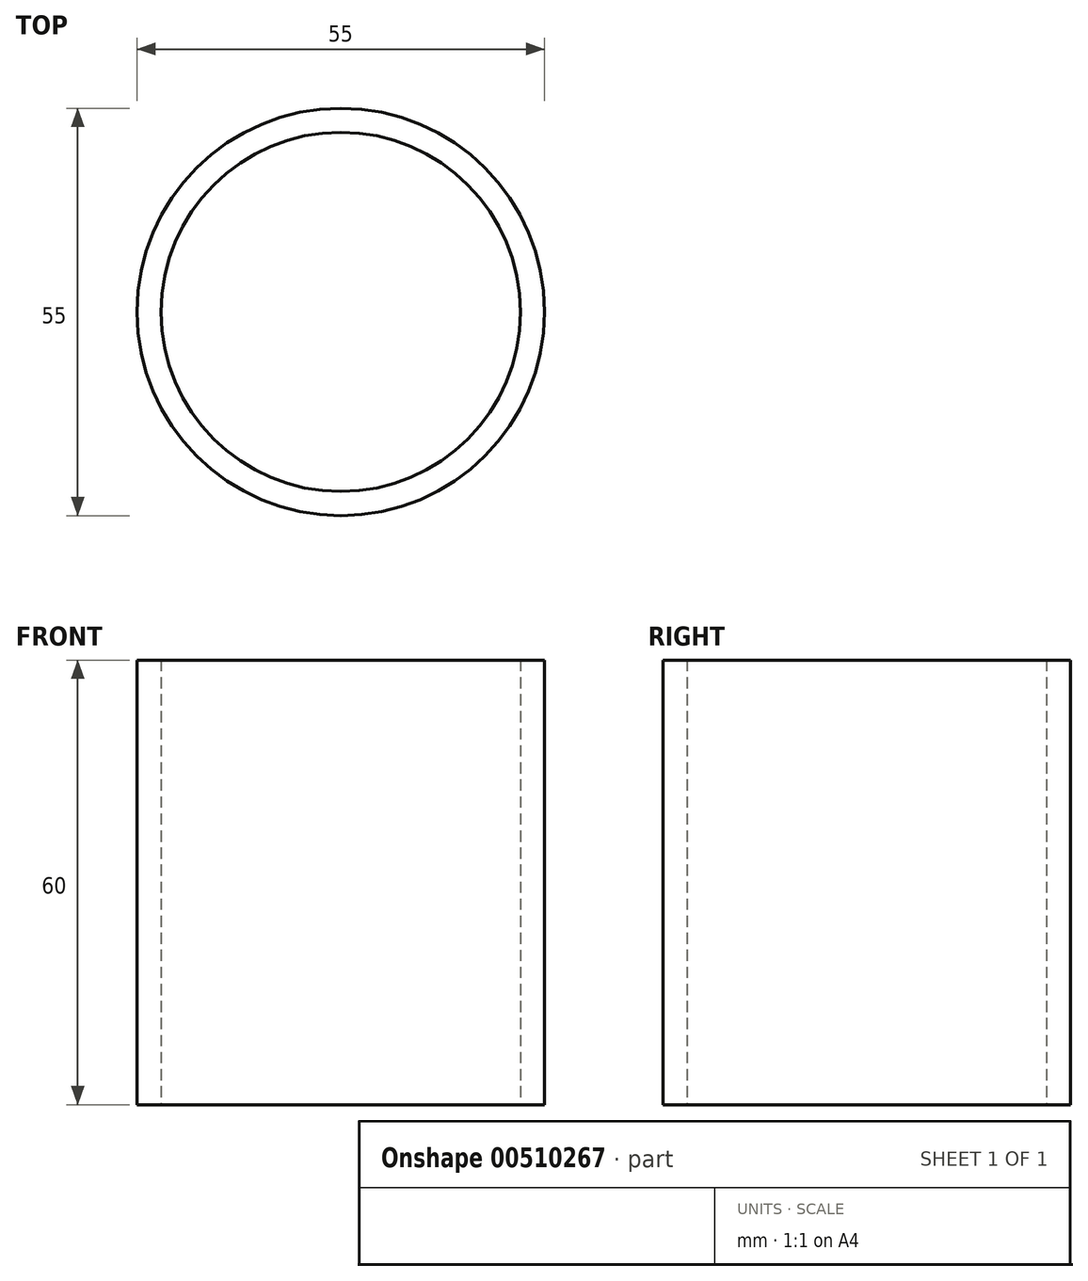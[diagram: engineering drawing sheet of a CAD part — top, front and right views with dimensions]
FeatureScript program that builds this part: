
annotation { "Feature Type Name" : "Feature", "Feature Type Description" : "" }
export const myFeature = defineFeature(function(context is Context, id is Id, definition is map)
    precondition{}
    {
        {
            var Q0;
            Q0=qCreatedBy(makeId("Top.planeOp"),FACE);
            var sketch = newSketch(context, id + "F0", { "sketchPlane" : qUnion([Q0])});
            skCircle(sketch, "E0", {"center": v(0, 0) * mm, "radius": 24.25 * mm});
            skCircle(sketch, "E1", {"center": v(0, 0) * mm, "radius": 27.5 * mm});
            skSolve(sketch);
        }
        {
            var Q0;
            Q0 = qSketchRegion(id + "F0", true);
            extrude(context, id + "F1", {"entities" : qUnion([Q0]), "depth" : 60 * mm});
        }
    });
